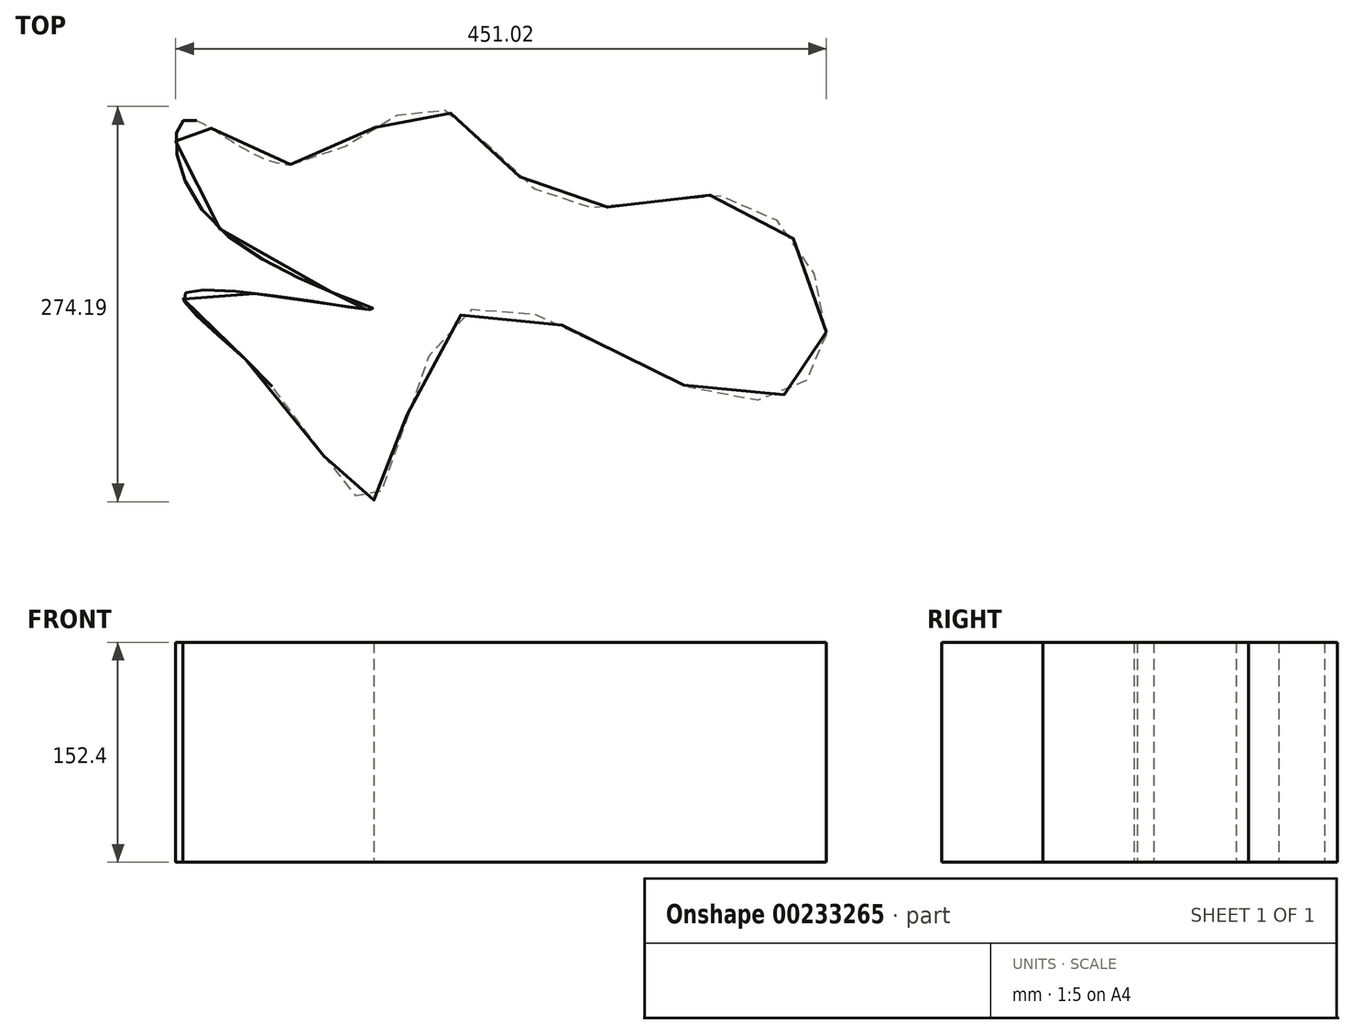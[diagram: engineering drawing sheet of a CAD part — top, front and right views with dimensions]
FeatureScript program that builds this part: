
annotation { "Feature Type Name" : "Feature", "Feature Type Description" : "" }
export const myFeature = defineFeature(function(context is Context, id is Id, definition is map)
    precondition{}
    {
        {
            var Q0;
            Q0=qCreatedBy(makeId("Top.planeOp"),FACE);
            var sketch = newSketch(context, id + "F0", { "sketchPlane" : qUnion([Q0])});
            skFitSpline(sketch, "E0", {"points": [v(-159.49, 116.17) * mm, v(-62.24, 156.4) * mm, v(26.07, 90.46) * mm, v(156.85, 90.46) * mm, v(210.5, -11.26) * mm, v(136.73, -44.8) * mm, v(-41, 12.21) * mm, v(-101.36, -116.33) * mm, v(-174.02, -35.85) * mm, v(-231.03, 27.86) * mm, v(-102.48, 15.57) * mm, v(-212.03, 74.8) * mm, v(-232.15, 147.47) * mm, v(-159.49, 116.17) * mm]});
            skSolve(sketch);
        }
        {
            var Q0;
            Q0 = qSketchRegion(id + "F0", true);
            extrude(context, id + "F1", {"entities" : qUnion([Q0]), "depth" : 152.4 * mm});
        }
    });
